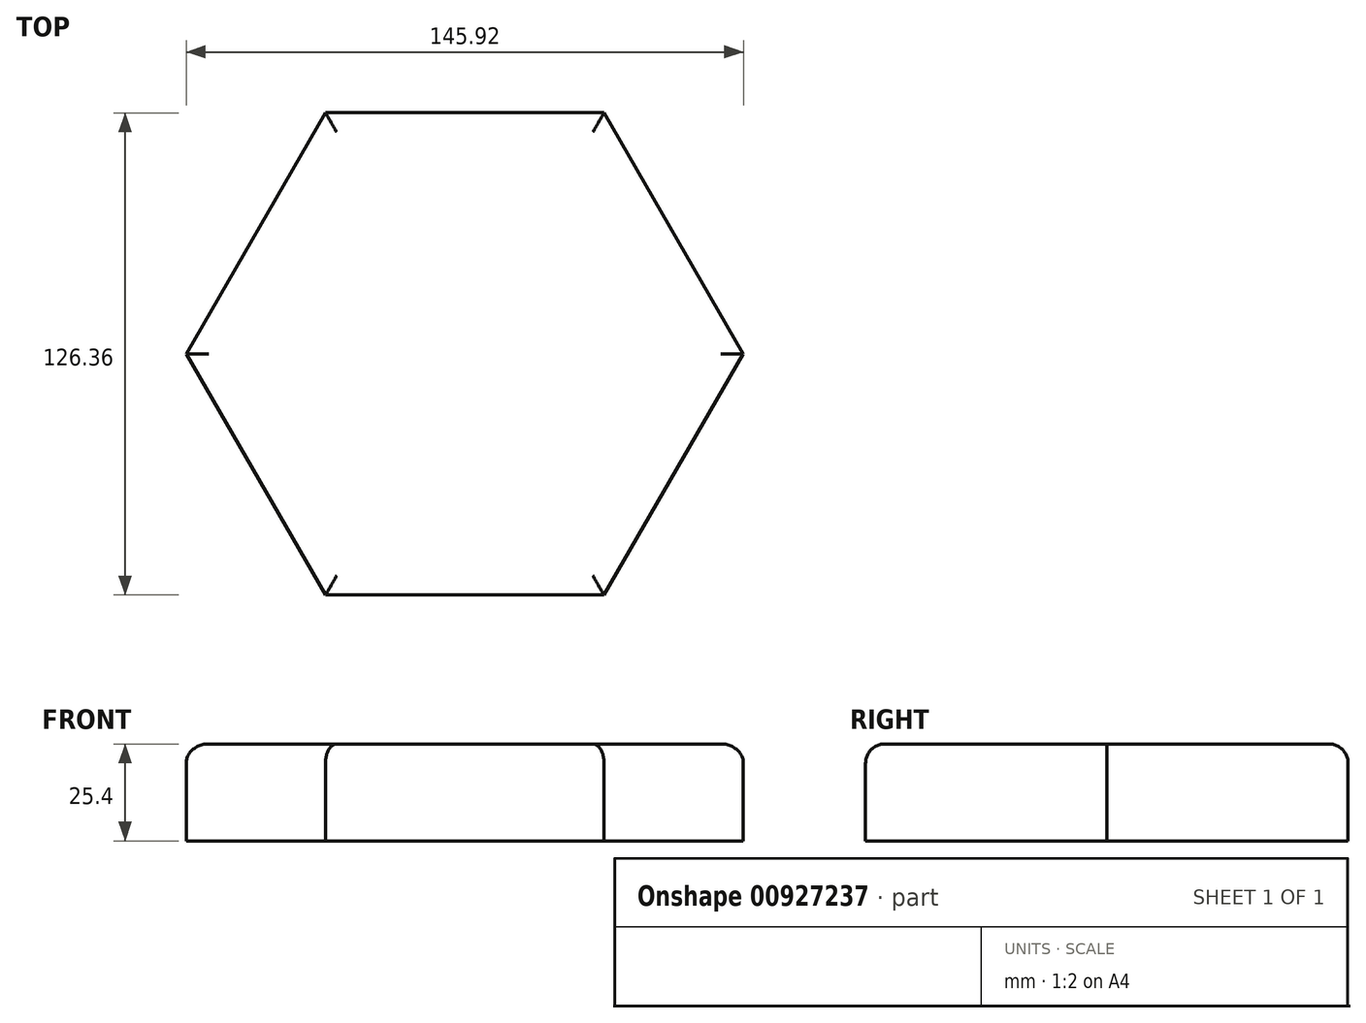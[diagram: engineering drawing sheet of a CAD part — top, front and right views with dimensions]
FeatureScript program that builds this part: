
annotation { "Feature Type Name" : "Feature", "Feature Type Description" : "" }
export const myFeature = defineFeature(function(context is Context, id is Id, definition is map)
    precondition{}
    {
        {
            var Q0;
            Q0=qCreatedBy(makeId("Top.planeOp"),FACE);
            var sketch = newSketch(context, id + "F0", { "sketchPlane" : qUnion([Q0])});
            skCircle(sketch, "E0.cCircle", {"center": v(0, 0) * mm, "radius": 63.18 * mm, "construction": true});
            skLineSegment(sketch, "E0.0", {"start": v(-36.48, 63.18) * mm, "end": v(36.48, 63.18) * mm});
            skLineSegment(sketch, "E0.1", {"start": v(36.48, 63.18) * mm, "end": v(72.96, 0) * mm});
            skLineSegment(sketch, "E0.2", {"start": v(72.96, 0) * mm, "end": v(36.48, -63.18) * mm});
            skLineSegment(sketch, "E0.3", {"start": v(36.48, -63.18) * mm, "end": v(-36.48, -63.18) * mm});
            skLineSegment(sketch, "E0.4", {"start": v(-36.48, -63.18) * mm, "end": v(-72.96, 0) * mm});
            skLineSegment(sketch, "E0.5", {"start": v(-72.96, 0) * mm, "end": v(-36.48, 63.18) * mm});
            skPoint(sketch, "E0.0.midPoint", {"position": v(0, 63.18) * mm});
            skSolve(sketch);
        }
        {
            var Q0;
            Q0=makeQuery(id+"F0.imprint","IMPRINT",FACE,{"disambiguationData":[TD([[makeQuery(id+"F0.imprint","IMPRINT",EDGE,{"derivedFrom":sQuery(id+"F0.wireOp",EDGE,"E0.0")}),-1.0]])]});
            extrude(context, id + "F1", {"entities" : qUnion([Q0]), "depth" : 25.4 * mm, "offsetDistance" : 25.4 * mm});
        }
        {
            var Q0;
            Q0=makeQuery(id+"F1.opExtrude","CAP_FACE",FACE,{"disambiguationData":[OSD([sQuery(id+"F0.wireOp",EDGE,"E0.0"),sQuery(id+"F0.wireOp",EDGE,"E0.1"),sQuery(id+"F0.wireOp",EDGE,"E0.2"),sQuery(id+"F0.wireOp",EDGE,"E0.3"),sQuery(id+"F0.wireOp",EDGE,"E0.4"),sQuery(id+"F0.wireOp",EDGE,"E0.5")])],"isStart":false});
            fillet(context, id + "F2", {"entities" : qUnion([Q0]), "radius" : 5.08 * mm, "tangentPropagation" : true, "allowEdgeOverflow" : false});
        }
    });
